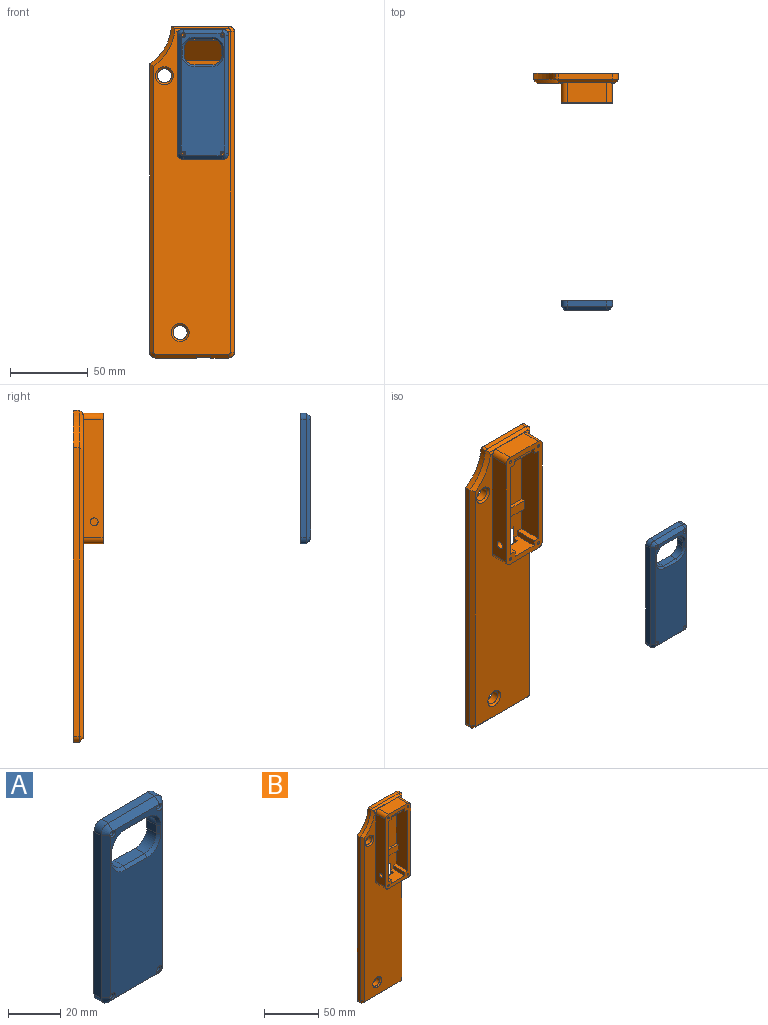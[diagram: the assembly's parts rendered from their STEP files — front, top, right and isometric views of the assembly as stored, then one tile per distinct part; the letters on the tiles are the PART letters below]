
ASSEMBLY  parts=2 mates=1
PART A: 42 faces, bbox 33x6.4x83.8 mm
  f0: plane 76.2x3.81mm, normal (1,0,0), area 290.3mm2, adj f1,f7,f9,f12
  f1: cylinder r=3.81mm len=3.81mm, axis (0,1,0), area 22.8mm2, adj f0,f2,f9,f10
  f2: plane 25.4x3.81mm, normal (0,0,1), area 96.8mm2, adj f1,f3,f9,f11
  f3: cylinder r=3.81mm len=3.81mm, axis (0,1,0), area 22.8mm2, adj f2,f4,f9,f13
  f4: plane 76.2x3.81mm, normal (-1,0,0), area 290.3mm2, adj f3,f5,f9,f15
  f5: cylinder r=3.81mm len=3.81mm, axis (0,1,0), area 22.8mm2, adj f4,f6,f9,f17
  f6: plane 25.4x3.81mm, normal (0,0,-1), area 96.8mm2, adj f5,f7,f9,f16
  f7: cylinder r=3.81mm len=3.81mm, axis (0,1,0), area 22.8mm2, adj f0,f6,f9,f14
  f8: plane 78.74x27.94mm, normal (0,-1,0), area 1712.1mm2, adj f11,f12,f15,f16,f26,f27,f28,f29
  f9: plane 83.82x33.02mm, normal (0,1,0), area 2378.9mm2, adj f0,f1,f2,f3,f4,f5,f6,f7
  f10: cone r=1.27mm half-angle=45deg, axis (0,1,0), area 13.8mm2, adj f1,f11,f12,f40
  f11: plane 25.4x2.54mm, normal (0,-0.71,0.71), area 90.9mm2, adj f2,f8,f10,f13,f40,f41
  f12: plane 76.2x2.54mm, normal (0.71,-0.71,0), area 273.4mm2, adj f0,f8,f10,f14,f39,f40
  f13: cone r=1.27mm half-angle=45deg, axis (0,1,0), area 13.8mm2, adj f3,f11,f15,f41
  f14: cone r=1.27mm half-angle=45deg, axis (0,1,0), area 13.8mm2, adj f7,f12,f16,f39
  f15: plane 76.2x2.54mm, normal (-0.71,-0.71,0), area 273.4mm2, adj f4,f8,f13,f17,f38,f41
  f16: plane 25.4x2.54mm, normal (0,-0.71,-0.71), area 90.9mm2, adj f6,f8,f14,f17,f38,f39
  f17: cone r=1.27mm half-angle=45deg, axis (0,1,0), area 13.8mm2, adj f5,f15,f16,f38
  f18: cylinder r=6.35mm len=6.35mm, axis (0,-1,0), area 50.7mm2, adj f9,f19,f25,f29
  f19: plane 11.43x5.08mm, normal (0,0,1), area 58.1mm2, adj f9,f18,f20,f31
  f20: cylinder r=6.35mm len=6.35mm, axis (0,-1,0), area 50.7mm2, adj f9,f19,f21,f33
  f21: plane 5.08x3.81mm, normal (-1,0,0), area 19.4mm2, adj f9,f20,f22,f32
  f22: cylinder r=6.35mm len=6.35mm, axis (0,-1,0), area 50.7mm2, adj f9,f21,f23,f30
  f23: plane 11.43x5.08mm, normal (0,0,-1), area 58.1mm2, adj f9,f22,f24,f28
  f24: cylinder r=6.35mm len=6.35mm, axis (0,-1,0), area 50.7mm2, adj f9,f23,f25,f26
  f25: plane 5.08x3.81mm, normal (1,0,0), area 19.4mm2, adj f9,f18,f24,f27
  f26: cone r=6.35mm half-angle=45deg, axis (0,-1,0), area 19.7mm2, adj f8,f24,f27,f28
  f27: plane 3.81x1.27mm, normal (0.71,-0.71,0), area 6.8mm2, adj f8,f25,f26,f29
  f28: plane 11.43x1.27mm, normal (0,-0.71,-0.71), area 20.5mm2, adj f8,f23,f26,f30
  f29: cone r=6.35mm half-angle=45deg, axis (0,-1,0), area 19.7mm2, adj f8,f18,f27,f31
  f30: cone r=6.35mm half-angle=45deg, axis (0,-1,0), area 19.7mm2, adj f8,f22,f28,f32
  f31: plane 11.43x1.27mm, normal (0,-0.71,0.71), area 20.5mm2, adj f8,f19,f29,f33
  f32: plane 3.81x1.27mm, normal (-0.71,-0.71,0), area 6.8mm2, adj f8,f21,f30,f33
  f33: cone r=6.35mm half-angle=45deg, axis (0,-1,0), area 19.7mm2, adj f8,f20,f31,f32
  f34: cylinder r=1mm len=5.72mm, axis (0,1,0), area 35.9mm2, adj f9,f40
  f35: cylinder r=1mm len=5.72mm, axis (0,1,0), area 35.9mm2, adj f9,f41
  f36: cylinder r=1mm len=5.72mm, axis (0,1,0), area 35.9mm2, adj f9,f38
  f37: cylinder r=1mm len=5.72mm, axis (0,1,0), area 35.9mm2, adj f9,f39
  f38: cone r=1.64mm half-angle=45deg, axis (0,-1,0), area 6.4mm2, adj f8,f15,f16,f17,f36
  f39: cone r=1.64mm half-angle=45deg, axis (0,-1,0), area 6.4mm2, adj f8,f12,f14,f16,f37
  f40: cone r=1.64mm half-angle=45deg, axis (0,-1,0), area 6.4mm2, adj f8,f10,f11,f12,f34
  f41: cone r=1.64mm half-angle=45deg, axis (0,-1,0), area 6.4mm2, adj f8,f11,f13,f15,f35
PART B: 71 faces, bbox 54.6x19.1x213.4 mm
  f0: plane 32.51x25.4mm, normal (0,-1,0), area 825.6mm2, adj f1,f5,f47,f61
  f1: plane 68.61x15.24mm, normal (-1,0,0), area 947.8mm2, adj f0,f4,f17,f47,f52,f59,f60,f61
  f2: plane 17.83x2.54mm, normal (0,0,-1), area 45.3mm2, adj f3,f17,f56,f58
  f3: plane 17.83x3.81mm, normal (0,-1,0), area 67.9mm2, adj f2,f47,f56,f58
  f4: plane 25.4x20.46mm, normal (0,-1,0), area 413.4mm2, adj f1,f5,f6,f45,f46,f50,f52,f53
  f5: plane 68.61x15.24mm, normal (1,0,0), area 928.2mm2, adj f0,f4,f17,f18,f47,f55,f57,f60
  f6: plane 17.2x15.24mm, normal (0,0,1), area 223.3mm2, adj f4,f17,f42,f43,f48,f53,f54
  f7: plane 26.61x3.81mm, normal (0,0,-1), area 93.2mm2, adj f8,f19,f29,f45,f51
  f8: plane 46.99x2.54mm, normal (0,-0.71,-0.71), area 162.3mm2, adj f7,f20,f28,f31,f32,f42,f43,f44
  f9: cylinder r=3.81mm len=12.7mm, axis (0,1,0), area 76mm2, adj f10,f16,f17,f28
  f10: plane 25.4x12.7mm, normal (0,0,-1), area 322.6mm2, adj f9,f11,f17,f28
  f11: cylinder r=3.81mm len=12.7mm, axis (0,1,0), area 76mm2, adj f10,f12,f17,f28
  f12: plane 76.2x12.7mm, normal (1,0,0), area 967.7mm2, adj f11,f13,f17,f28
  f13: cylinder r=3.81mm len=13.36mm, axis (0,1,0), area 77.6mm2, adj f12,f14,f17,f28,f37
  f14: plane 25.4x13.36mm, normal (0,0,1), area 339.3mm2, adj f13,f15,f17,f37
  f15: cylinder r=3.81mm len=13.36mm, axis (0,1,0), area 77.6mm2, adj f14,f16,f17,f28,f37
  f16: plane 76.2x12.7mm, normal (-1,0,0), area 948.1mm2, adj f9,f15,f17,f18,f28
  f17: plane 83.82x33.02mm, normal (0,-1,0), area 867.1mm2, adj f1,f2,f5,f6,f9,f10,f11,f12
  f18: cylinder r=2.5mm len=5mm, axis (-1,0,0), area 59.8mm2, adj f5,f16
  f19: cylinder r=3.81mm len=3.81mm, axis (0,1,0), area 22.8mm2, adj f7,f27,f29,f31
  f20: plane 11.38x3.81mm, normal (0,0,-1), area 35.2mm2, adj f8,f21,f29,f46,f49
  f21: cylinder r=3.81mm len=3.81mm, axis (0,1,0), area 22.8mm2, adj f20,f22,f29,f32
  f22: plane 205.74x3.81mm, normal (1,0,0), area 783.9mm2, adj f21,f23,f29,f33
  f23: cylinder r=3.81mm len=3.81mm, axis (0,1,0), area 22.8mm2, adj f22,f24,f29,f35
  f24: plane 34.74x3.81mm, normal (0,0,1), area 132.3mm2, adj f23,f25,f29,f34
  f25: cylinder r=3.81mm len=4.17mm, axis (0,1,0), area 8.2mm2, adj f24,f26,f29,f34,f36
  f26: cylinder r=31.03mm len=23.84mm, axis (0,1,0), area 109.3mm2, adj f25,f27,f29,f36
  f27: plane 185.16x3.81mm, normal (-1,0,0), area 705.5mm2, adj f19,f26,f29,f30
  f28: plane 207.23x49.53mm, normal (0,-1,0), area 7147.6mm2, adj f8,f9,f10,f11,f12,f13,f15,f16
  f29: plane 213.36x54.61mm, normal (0,1,0), area 8440.1mm2, adj f7,f19,f20,f21,f22,f23,f24,f25
  f30: plane 185.16x2.54mm, normal (-0.71,-0.71,0), area 662.7mm2, adj f27,f28,f31,f36
  f31: cone r=1.27mm half-angle=45deg, axis (0,1,0), area 14.3mm2, adj f8,f19,f28,f30
  f32: cone r=1.27mm half-angle=45deg, axis (0,1,0), area 14.3mm2, adj f8,f21,f28,f33
  f33: plane 205.74x2.54mm, normal (0.71,-0.71,0), area 739mm2, adj f22,f28,f32,f35
  f34: plane 36.35x1.8mm, normal (0,-0.71,0.71), area 90.7mm2, adj f24,f25,f35,f36,f37
  f35: cone r=1.27mm half-angle=45deg, axis (0,1,0), area 13mm2, adj f23,f28,f33,f34,f37
  f36: cone r=31.03mm half-angle=45deg, axis (0,-1,0), area 101.9mm2, adj f25,f26,f28,f30,f34,f37
  f37: plane 36.33x1.81mm, normal (0,-0.92,0.38), area 18.6mm2, adj f13,f14,f15,f28,f34,f35,f36
  f38: cylinder r=4.5mm len=9mm, axis (0,1,0), area 143.6mm2, adj f29,f41
  f39: cylinder r=4.5mm len=9mm, axis (0,1,0), area 143.6mm2, adj f29,f40
  f40: cone r=5.77mm half-angle=45deg, axis (0,-1,0), area 57.9mm2, adj f28,f39
  f41: cone r=5.77mm half-angle=45deg, axis (0,-1,0), area 57.9mm2, adj f28,f38
  f42: plane 131.34x4.32mm, normal (1,0,0), area 73.9mm2, adj f6,f8,f44,f45,f48
  f43: plane 131.34x4.32mm, normal (-1,0,0), area 73.9mm2, adj f6,f8,f44,f46,f48
  f44: plane 127.03x9mm, normal (0,1,0), area 1143.2mm2, adj f8,f42,f43,f48
  f45: plane 142.39x2.69mm, normal (0.71,0.71,0), area 537.4mm2, adj f4,f7,f42,f50,f51
  f46: plane 142.39x2.69mm, normal (-0.71,0.71,0), area 537.4mm2, adj f4,f20,f43,f49,f50
  f47: plane 25.4x12.7mm, normal (0,-0.71,-0.71), area 456.2mm2, adj f0,f1,f3,f5,f57,f59
  f48: plane 9x3.81mm, normal (0,0.71,0.71), area 48.5mm2, adj f6,f42,f43,f44
  f49: plane 143.51x2.69mm, normal (-0.38,0.92,0), area 416.9mm2, adj f20,f29,f46,f50
  f50: plane 19.78x3.81mm, normal (0,0.71,-0.71), area 71.5mm2, adj f4,f29,f45,f46,f49,f51
  f51: plane 143.51x2.69mm, normal (0.38,0.92,0), area 416.9mm2, adj f7,f29,f45,f50
  f52: plane 15.24x3.79mm, normal (0,0,1), area 57.7mm2, adj f1,f4,f17,f53
  f53: plane 15.24x3.78mm, normal (-1,0,0), area 57.7mm2, adj f4,f6,f17,f52
  f54: plane 15.24x3.78mm, normal (1,0,0), area 57.7mm2, adj f4,f6,f17,f55
  f55: plane 15.24x4.41mm, normal (0,0,1), area 67.3mm2, adj f4,f5,f17,f54
  f56: plane 3.81x2.54mm, normal (1,0,0), area 9.7mm2, adj f2,f3,f17,f57
  f57: plane 3.78x2.54mm, normal (0,0,-1), area 9.6mm2, adj f5,f17,f47,f56
  f58: plane 3.81x2.54mm, normal (-1,0,0), area 9.7mm2, adj f2,f3,f17,f59
  f59: plane 3.78x2.54mm, normal (0,0,-1), area 9.6mm2, adj f1,f17,f47,f58
  f60: plane 25.4x2.54mm, normal (0,0,-1), area 64.5mm2, adj f1,f4,f5,f62
  f61: plane 25.4x2.54mm, normal (0,0,1), area 64.5mm2, adj f0,f1,f5,f62
  f62: plane 25.4x6.73mm, normal (0,-1,0), area 170.9mm2, adj f1,f5,f60,f61
  f63: cone r=0mm half-angle=59deg, axis (0,-1,0), area 3.7mm2, adj f64
  f64: cylinder r=1mm len=10.16mm, axis (0,-1,0), area 63.8mm2, adj f17,f63
  f65: cone r=0mm half-angle=59deg, axis (0,-1,0), area 3.7mm2, adj f66
  f66: cylinder r=1mm len=10.16mm, axis (0,-1,0), area 63.8mm2, adj f17,f65
  f67: cone r=0mm half-angle=59deg, axis (0,-1,0), area 3.7mm2, adj f68
  f68: cylinder r=1mm len=10.16mm, axis (0,-1,0), area 63.8mm2, adj f17,f67
  f69: cone r=0mm half-angle=59deg, axis (0,-1,0), area 3.7mm2, adj f70
  f70: cylinder r=1mm len=10.16mm, axis (0,-1,0), area 63.8mm2, adj f17,f69
PLACE A t=(15.79,-117.53,62.34)mm
PLACE B t=(6.73,28.52,-4.23)mm fixed
MATE slider B.f17 <-> A.f9  axis (0,-1,0) through (17,9.47,133.93)mm
